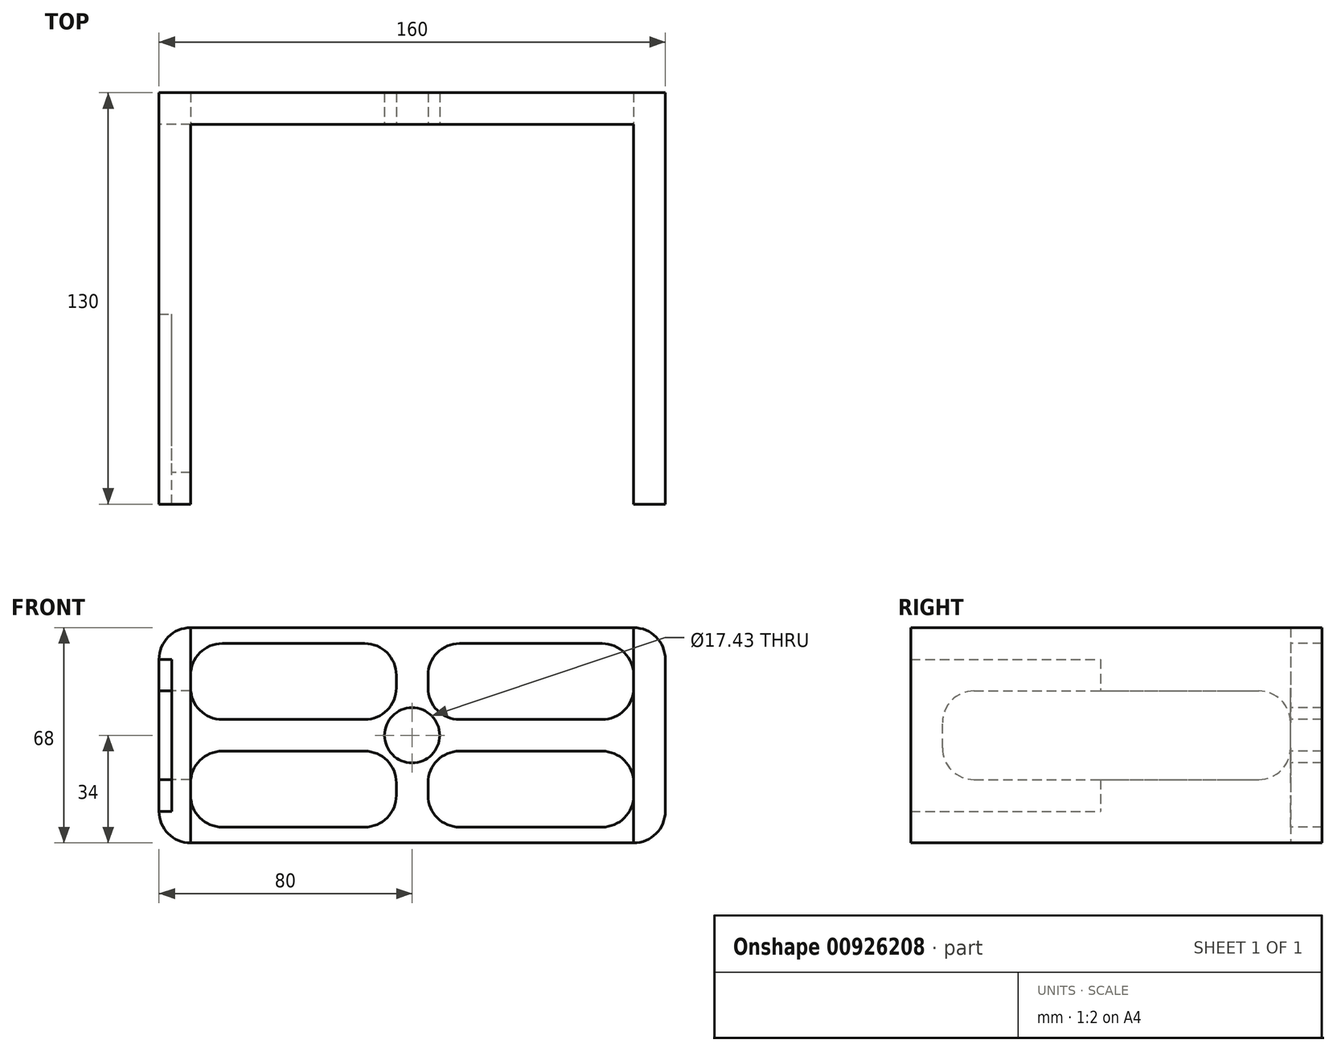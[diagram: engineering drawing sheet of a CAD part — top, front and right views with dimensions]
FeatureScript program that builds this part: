
annotation { "Feature Type Name" : "Feature", "Feature Type Description" : "" }
export const myFeature = defineFeature(function(context is Context, id is Id, definition is map)
    precondition{}
    {
        {
            var Q0;
            Q0=qCreatedBy(makeId("Front.planeOp"),FACE);
            var sketch = newSketch(context, id + "F0", { "sketchPlane" : qUnion([Q0])});
            skLineSegment(sketch, "E0.bottom", {"start": v(70, -34) * mm, "end": v(-70, -34) * mm});
            skLineSegment(sketch, "E0.top", {"start": v(70, 34) * mm, "end": v(-70, 34) * mm});
            skLineSegment(sketch, "E0.left", {"start": v(80, -24) * mm, "end": v(80, 24) * mm});
            skLineSegment(sketch, "E0.right", {"start": v(-80, -24) * mm, "end": v(-80, 24) * mm});
            skPoint(sketch, "E0.middle", {"position": v(0, 0) * mm});
            skPoint(sketch, "E1.visualSharp", {"position": v(-80, 34) * mm});
            skArc(sketch, "E1.filletArc", {"start": v(-70, 34) * mm, "mid": v(-77.07, 31.07) * mm, "end": v(-80, 24) * mm});
            skPoint(sketch, "E2.visualSharp", {"position": v(-80, -34) * mm});
            skArc(sketch, "E2.filletArc", {"start": v(-80, -24) * mm, "mid": v(-77.07, -31.07) * mm, "end": v(-70, -34) * mm});
            skPoint(sketch, "E3.visualSharp", {"position": v(80, -34) * mm});
            skArc(sketch, "E3.filletArc", {"start": v(70, -34) * mm, "mid": v(77.07, -31.07) * mm, "end": v(80, -24) * mm});
            skPoint(sketch, "E4.visualSharp", {"position": v(80, 34) * mm});
            skArc(sketch, "E4.filletArc", {"start": v(80, 24) * mm, "mid": v(77.07, 31.07) * mm, "end": v(70, 34) * mm});
            skSolve(sketch);
        }
        {
            var Q0;
            Q0 = qSketchRegion(id + "F0", true);
            extrude(context, id + "F1", {"entities" : qUnion([Q0]), "depth" : 10 * mm, "offsetDistance" : 25.4 * mm});
        }
        {
            var Q0;
            Q0=makeQuery(id+"F1.opExtrude","CAP_FACE",FACE,{"disambiguationData":[OSD([sQuery(id+"F0.wireOp",EDGE,"E0.bottom"),sQuery(id+"F0.wireOp",EDGE,"E0.top"),sQuery(id+"F0.wireOp",EDGE,"E0.left"),sQuery(id+"F0.wireOp",EDGE,"E0.right"),sQuery(id+"F0.wireOp",EDGE,"E1.filletArc"),sQuery(id+"F0.wireOp",EDGE,"E2.filletArc"),sQuery(id+"F0.wireOp",EDGE,"E3.filletArc"),sQuery(id+"F0.wireOp",EDGE,"E4.filletArc")])],"isStart":false});
            var sketch = newSketch(context, id + "F2", { "sketchPlane" : qUnion([Q0])});
            skLineSegment(sketch, "E5.bottom", {"start": v(60, 5) * mm, "end": v(15, 5) * mm});
            skLineSegment(sketch, "E5.top", {"start": v(60, 29) * mm, "end": v(15, 29) * mm});
            skLineSegment(sketch, "E5.left", {"start": v(70, 15) * mm, "end": v(70, 19) * mm});
            skLineSegment(sketch, "E5.right", {"start": v(5, 15) * mm, "end": v(5, 19) * mm});
            skPoint(sketch, "E6.visualSharp", {"position": v(70, 29) * mm});
            skArc(sketch, "E6.filletArc", {"start": v(70, 19) * mm, "mid": v(67.07, 26.07) * mm, "end": v(60, 29) * mm});
            skPoint(sketch, "E7.visualSharp", {"position": v(70, 5) * mm});
            skArc(sketch, "E7.filletArc", {"start": v(60, 5) * mm, "mid": v(67.07, 7.93) * mm, "end": v(70, 15) * mm});
            skPoint(sketch, "E8.visualSharp", {"position": v(5, 5) * mm});
            skArc(sketch, "E8.filletArc", {"start": v(5, 15) * mm, "mid": v(7.93, 7.93) * mm, "end": v(15, 5) * mm});
            skPoint(sketch, "E9.visualSharp", {"position": v(5, 29) * mm});
            skArc(sketch, "E9.filletArc", {"start": v(15, 29) * mm, "mid": v(7.93, 26.07) * mm, "end": v(5, 19) * mm});
            skArc(sketch, "E10.MirrorCS", {"start": v(60, -5) * mm, "mid": v(67.07, -7.93) * mm, "end": v(70, -15) * mm});
            skPoint(sketch, "E11.MirrorP", {"position": v(5, -5) * mm});
            skArc(sketch, "E12.MirrorCS", {"start": v(5, -15) * mm, "mid": v(7.93, -7.93) * mm, "end": v(15, -5) * mm});
            skArc(sketch, "E13.MirrorCS", {"start": v(15, -29) * mm, "mid": v(7.93, -26.07) * mm, "end": v(5, -19) * mm});
            skPoint(sketch, "E14.MirrorP", {"position": v(70, -5) * mm});
            skArc(sketch, "E15.MirrorCS", {"start": v(70, -19) * mm, "mid": v(67.07, -26.07) * mm, "end": v(60, -29) * mm});
            skLineSegment(sketch, "E16.MirrorCS", {"start": v(60, -29) * mm, "end": v(15, -29) * mm});
            skLineSegment(sketch, "E17.MirrorCS", {"start": v(60, -5) * mm, "end": v(15, -5) * mm});
            skPoint(sketch, "E18.MirrorP", {"position": v(70, -29) * mm});
            skPoint(sketch, "E19.MirrorP", {"position": v(5, -29) * mm});
            skLineSegment(sketch, "E20.MirrorCS", {"start": v(70, -15) * mm, "end": v(70, -19) * mm});
            skLineSegment(sketch, "E21.MirrorCS", {"start": v(5, -15) * mm, "end": v(5, -19) * mm});
            skPoint(sketch, "E22.MirrorP", {"position": v(-70, -5) * mm});
            skArc(sketch, "E23.MirrorCS", {"start": v(-60, -5) * mm, "mid": v(-67.07, -7.93) * mm, "end": v(-70, -15) * mm});
            skArc(sketch, "E24.MirrorCS", {"start": v(-15, 29) * mm, "mid": v(-7.93, 26.07) * mm, "end": v(-5, 19) * mm});
            skLineSegment(sketch, "E25.MirrorCS", {"start": v(-60, 5) * mm, "end": v(-15, 5) * mm});
            skArc(sketch, "E26.MirrorCS", {"start": v(-70, 19) * mm, "mid": v(-67.07, 26.07) * mm, "end": v(-60, 29) * mm});
            skPoint(sketch, "E27.MirrorP", {"position": v(-70, 29) * mm});
            skLineSegment(sketch, "E28.MirrorCS", {"start": v(-60, 29) * mm, "end": v(-15, 29) * mm});
            skPoint(sketch, "E29.MirrorP", {"position": v(-70, 5) * mm});
            skArc(sketch, "E30.MirrorCS", {"start": v(-15, -29) * mm, "mid": v(-7.93, -26.07) * mm, "end": v(-5, -19) * mm});
            skPoint(sketch, "E31.MirrorP", {"position": v(-5, 5) * mm});
            skArc(sketch, "E32.MirrorCS", {"start": v(-5, 15) * mm, "mid": v(-7.93, 7.93) * mm, "end": v(-15, 5) * mm});
            skArc(sketch, "E33.MirrorCS", {"start": v(-70, -19) * mm, "mid": v(-67.07, -26.07) * mm, "end": v(-60, -29) * mm});
            skArc(sketch, "E34.MirrorCS", {"start": v(-5, -15) * mm, "mid": v(-7.93, -7.93) * mm, "end": v(-15, -5) * mm});
            skPoint(sketch, "E35.MirrorP", {"position": v(-5, -29) * mm});
            skArc(sketch, "E36.MirrorCS", {"start": v(-60, 5) * mm, "mid": v(-67.07, 7.93) * mm, "end": v(-70, 15) * mm});
            skLineSegment(sketch, "E37.MirrorCS", {"start": v(-60, -5) * mm, "end": v(-15, -5) * mm});
            skPoint(sketch, "E38.MirrorP", {"position": v(-5, -5) * mm});
            skPoint(sketch, "E39.MirrorP", {"position": v(-70, -29) * mm});
            skLineSegment(sketch, "E40.MirrorCS", {"start": v(-60, -29) * mm, "end": v(-15, -29) * mm});
            skPoint(sketch, "E41.MirrorP", {"position": v(-5, 29) * mm});
            skCircle(sketch, "E42", {"center": v(0, 0) * mm, "radius": 8.71 * mm});
            skLineSegment(sketch, "E43", {"start": v(-70, 19) * mm, "end": v(-70, 15) * mm});
            skLineSegment(sketch, "E44", {"start": v(-70, -15) * mm, "end": v(-70, -19) * mm});
            skLineSegment(sketch, "E45", {"start": v(-5, -15) * mm, "end": v(-5, -19) * mm});
            skLineSegment(sketch, "E46", {"start": v(-5, 19) * mm, "end": v(-5, 15) * mm});
            skSolve(sketch);
        }
        {
            var Q0;
            Q0 = qSketchRegion(id + "F2", true);
            extrude(context, id + "F3", {"entities" : qUnion([Q0]), "operationType" : NewBodyOperationType.REMOVE, "oppositeDirection" : true, "depth" : 11 * mm, "offsetDistance" : 25.4 * mm});
        }
        {
            var Q0;
            Q0 = qSketchRegion(id + "F2", true);
            extrude(context, id + "F4", {"entities" : qUnion([Q0]), "operationType" : NewBodyOperationType.REMOVE, "oppositeDirection" : true, "depth" : 11 * mm, "offsetDistance" : 25.4 * mm});
        }
        {
            var Q0;
            Q0=makeQuery(id+"F1.opExtrude","CAP_FACE",FACE,{"disambiguationData":[OSD([sQuery(id+"F0.wireOp",EDGE,"E0.bottom"),sQuery(id+"F0.wireOp",EDGE,"E0.top"),sQuery(id+"F0.wireOp",EDGE,"E0.left"),sQuery(id+"F0.wireOp",EDGE,"E0.right"),sQuery(id+"F0.wireOp",EDGE,"E1.filletArc"),sQuery(id+"F0.wireOp",EDGE,"E2.filletArc"),sQuery(id+"F0.wireOp",EDGE,"E3.filletArc"),sQuery(id+"F0.wireOp",EDGE,"E4.filletArc")])],"isStart":false});
            var sketch = newSketch(context, id + "F5", { "sketchPlane" : qUnion([Q0])});
            skLineSegment(sketch, "E47.bottom", {"start": v(70, -34) * mm, "end": v(70, -34) * mm});
            skLineSegment(sketch, "E47.top", {"start": v(70, 34) * mm, "end": v(70, 34) * mm});
            skLineSegment(sketch, "E47.left", {"start": v(70, -34) * mm, "end": v(70, 34) * mm});
            skLineSegment(sketch, "E47.right", {"start": v(80, -24) * mm, "end": v(80, 24) * mm});
            skPoint(sketch, "E48.visualSharp", {"position": v(80, -34) * mm});
            skArc(sketch, "E48.filletArc", {"start": v(70, -34) * mm, "mid": v(77.07, -31.07) * mm, "end": v(80, -24) * mm});
            skPoint(sketch, "E49.visualSharp", {"position": v(80, 34) * mm});
            skArc(sketch, "E49.filletArc", {"start": v(80, 24) * mm, "mid": v(77.07, 31.07) * mm, "end": v(70, 34) * mm});
            skLineSegment(sketch, "E50.MirrorCS", {"start": v(-70, -34) * mm, "end": v(-70, 34) * mm});
            skLineSegment(sketch, "E51.MirrorCS", {"start": v(-80, -24) * mm, "end": v(-80, 24) * mm});
            skArc(sketch, "E52.MirrorCS", {"start": v(-80, 24) * mm, "mid": v(-77.07, 31.07) * mm, "end": v(-70, 34) * mm});
            skPoint(sketch, "E53.MirrorP", {"position": v(-80, 34) * mm});
            skPoint(sketch, "E54.MirrorP", {"position": v(-80, -34) * mm});
            skArc(sketch, "E55.MirrorCS", {"start": v(-70, -34) * mm, "mid": v(-77.07, -31.07) * mm, "end": v(-80, -24) * mm});
            skSolve(sketch);
        }
        {
            var Q0;
            Q0 = qSketchRegion(id + "F5", true);
            extrude(context, id + "F6", {"entities" : qUnion([Q0]), "operationType" : NewBodyOperationType.ADD, "depth" : 120 * mm, "offsetDistance" : 25.4 * mm});
        }
        {
            var Q0;
            Q0=makeQuery(id+"F6.boolean.opBoolean","MERGE",FACE,{"derivedFrom":[makeQuery(id+"F1.opExtrude","SWEPT_FACE",FACE,{"disambiguationData":[OSD([sQuery(id+"F0.wireOp",EDGE,"E0.right")])]}),makeQuery(id+"F6.opExtrude","SWEPT_FACE",FACE,{"disambiguationData":[OSD([sQuery(id+"F5.wireOp",EDGE,"E51.MirrorCS")])]})]});
            var sketch = newSketch(context, id + "F7", { "sketchPlane" : qUnion([Q0])});
            skLineSegment(sketch, "E56.bottom", {"start": v(130, 24) * mm, "end": v(70, 24) * mm});
            skLineSegment(sketch, "E56.top", {"start": v(130, -24) * mm, "end": v(70, -24) * mm});
            skLineSegment(sketch, "E56.left", {"start": v(130, 24) * mm, "end": v(130, -24) * mm});
            skLineSegment(sketch, "E56.right", {"start": v(70, 24) * mm, "end": v(70, -24) * mm});
            skSolve(sketch);
        }
        {
            var Q0;
            Q0 = qSketchRegion(id + "F7", true);
            extrude(context, id + "F8", {"entities" : qUnion([Q0]), "operationType" : NewBodyOperationType.REMOVE, "oppositeDirection" : true, "depth" : 4 * mm, "offsetDistance" : 25.4 * mm});
        }
        {
            var Q0;
            Q0=makeQuery(id+"F6.boolean.opBoolean","MERGE",FACE,{"derivedFrom":[makeQuery(id+"F1.opExtrude","SWEPT_FACE",FACE,{"disambiguationData":[OSD([sQuery(id+"F0.wireOp",EDGE,"E0.right")])]}),makeQuery(id+"F6.opExtrude","SWEPT_FACE",FACE,{"disambiguationData":[OSD([sQuery(id+"F5.wireOp",EDGE,"E51.MirrorCS")])]})]});
            var sketch = newSketch(context, id + "F9", { "sketchPlane" : qUnion([Q0])});
            skLineSegment(sketch, "E57.bottom", {"start": v(110, -14) * mm, "end": v(20, -14) * mm});
            skLineSegment(sketch, "E57.top", {"start": v(110, 14) * mm, "end": v(20, 14) * mm});
            skLineSegment(sketch, "E57.left", {"start": v(120, -4) * mm, "end": v(120, 4) * mm});
            skLineSegment(sketch, "E57.right", {"start": v(10, -4) * mm, "end": v(10, 4) * mm});
            skPoint(sketch, "E58.visualSharp", {"position": v(10, -14) * mm});
            skArc(sketch, "E58.filletArc", {"start": v(10, -4) * mm, "mid": v(12.93, -11.07) * mm, "end": v(20, -14) * mm});
            skPoint(sketch, "E59.visualSharp", {"position": v(10, 14) * mm});
            skArc(sketch, "E59.filletArc", {"start": v(20, 14) * mm, "mid": v(12.93, 11.07) * mm, "end": v(10, 4) * mm});
            skPoint(sketch, "E60.visualSharp", {"position": v(120, 14) * mm});
            skArc(sketch, "E60.filletArc", {"start": v(120, 4) * mm, "mid": v(117.07, 11.07) * mm, "end": v(110, 14) * mm});
            skPoint(sketch, "E61.visualSharp", {"position": v(120, -14) * mm});
            skArc(sketch, "E61.filletArc", {"start": v(110, -14) * mm, "mid": v(117.07, -11.07) * mm, "end": v(120, -4) * mm});
            skSolve(sketch);
        }
        {
            var Q0;
            Q0 = qSketchRegion(id + "F9", true);
            extrude(context, id + "F10", {"entities" : qUnion([Q0]), "operationType" : NewBodyOperationType.REMOVE, "oppositeDirection" : true, "depth" : 10 * mm, "offsetDistance" : 25.4 * mm});
        }
    });
